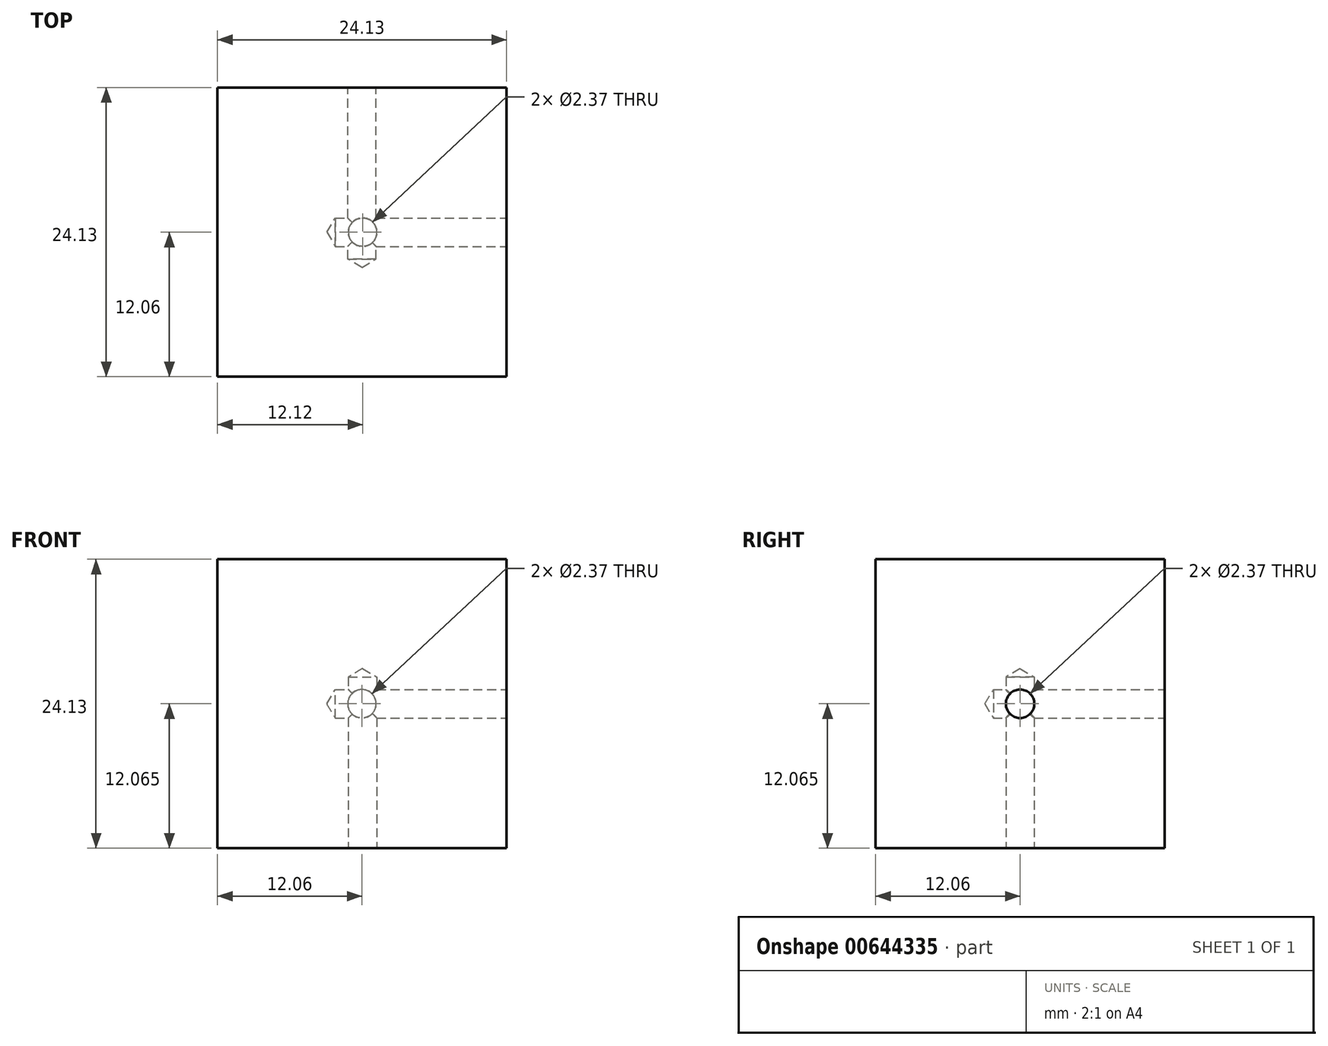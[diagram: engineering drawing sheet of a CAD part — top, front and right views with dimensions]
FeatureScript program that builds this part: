
annotation { "Feature Type Name" : "Feature", "Feature Type Description" : "" }
export const myFeature = defineFeature(function(context is Context, id is Id, definition is map)
    precondition{}
    {
        {
            var Q0;
            Q0=qCreatedBy(makeId("Top.planeOp"),FACE);
            var sketch = newSketch(context, id + "F0", { "sketchPlane" : qUnion([Q0])});
            skLineSegment(sketch, "E0.bottom", {"start": v(-12.06, 12.07) * mm, "end": v(12.07, 12.07) * mm});
            skLineSegment(sketch, "E0.top", {"start": v(-12.06, -12.07) * mm, "end": v(12.06, -12.07) * mm});
            skLineSegment(sketch, "E0.left", {"start": v(-12.06, 12.07) * mm, "end": v(-12.07, -12.06) * mm});
            skLineSegment(sketch, "E0.right", {"start": v(12.06, 12.07) * mm, "end": v(12.06, -12.06) * mm});
            skPoint(sketch, "E0.middle", {"position": v(0, 0) * mm});
            skSolve(sketch);
        }
        {
            var Q0;
            Q0=makeQuery(id+"F0.imprint","IMPRINT",FACE,{"disambiguationData":[TD([[makeQuery(id+"F0.imprint","IMPRINT",EDGE,{"derivedFrom":sQuery(id+"F0.wireOp",EDGE,"E0.bottom")}),-1.0]])]});
            extrude(context, id + "F1", {"entities" : qUnion([Q0]), "depth" : 24.13 * mm, "offsetDistance" : 25.4 * mm});
        }
        {
            var Q0;
            Q0=makeQuery(id+"F1.opExtrude","SWEPT_FACE",FACE,{"disambiguationData":[OSD([sQuery(id+"F0.wireOp",EDGE,"E0.right")])]});
            var sketch = newSketch(context, id + "F2", { "sketchPlane" : qUnion([Q0])});
            skLineSegment(sketch, "E1", {"start": v(0, 0) * mm, "end": v(0, 12.07) * mm});
            skPoint(sketch, "E1.endSnap0", {"position": v(0, 0) * mm});
            skCircle(sketch, "E2", {"center": v(0, 12.07) * mm, "radius": 1.2 * mm});
            skSolve(sketch);
        }
        {
            var Q0;
            Q0=sQuery(id+"F2.wireOp",VERTEX,"E2.center");
            var Q1;
            Q1=makeQuery(id+"F1.opExtrude","SWEPT_BODY",BODY,{"disambiguationData":[OSD([sQuery(id+"F0.wireOp",EDGE,"E0.bottom"),sQuery(id+"F0.wireOp",EDGE,"E0.top"),sQuery(id+"F0.wireOp",EDGE,"E0.left"),sQuery(id+"F0.wireOp",EDGE,"E0.right")])]});
            hole(context, id + "F3", {"style" : HoleStyle.SIMPLE, "endStyle" : HoleEndStyle.BLIND, "standardTappedOrClearance" : lookupTablePath({ "standard" : "ANSI", "engagement" : "75%", "pitch" : "48 tpi", "size" : "#4", "type" : "Tapped" }), "standardBlindInLast" : lookupTablePath({ "standard" : "ANSI", "engagement" : "75%", "pitch" : "48 tpi", "size" : "#4", "type" : "Tapped" }), "holeDiameter" : 2.37 * mm, "majorDiameter" : 2.84 * mm, "showTappedDepth" : true, "holeDepth" : 14.29 * mm, "isTappedThrough" : true, "tappedDepth" : 12.7 * mm, "tapClearance" : 3, "locations" : qUnion([Q0]), "scope" : qUnion([Q1])});
        }
        {
            var Q0;
            Q0=makeQuery(id+"F1.opExtrude","CAP_FACE",FACE,{"disambiguationData":[OSD([sQuery(id+"F0.wireOp",EDGE,"E0.bottom"),sQuery(id+"F0.wireOp",EDGE,"E0.top"),sQuery(id+"F0.wireOp",EDGE,"E0.left"),sQuery(id+"F0.wireOp",EDGE,"E0.right")])],"isStart":true});
            var sketch = newSketch(context, id + "F4", { "sketchPlane" : qUnion([Q0])});
            skLineSegment(sketch, "E3", {"start": v(0.06, 0) * mm, "end": v(0.06, -12.07) * mm});
            skCircle(sketch, "E4", {"center": v(0, 0) * mm, "radius": 1.2 * mm});
            skSolve(sketch);
        }
        {
            var Q0;
            Q0=sQuery(id+"F4.wireOp",VERTEX,"E3.start");
            var Q1;
            Q1=makeQuery(id+"F1.opExtrude","SWEPT_BODY",BODY,{"disambiguationData":[OSD([sQuery(id+"F0.wireOp",EDGE,"E0.bottom"),sQuery(id+"F0.wireOp",EDGE,"E0.top"),sQuery(id+"F0.wireOp",EDGE,"E0.left"),sQuery(id+"F0.wireOp",EDGE,"E0.right")])]});
            hole(context, id + "F5", {"style" : HoleStyle.SIMPLE, "endStyle" : HoleEndStyle.BLIND, "standardTappedOrClearance" : lookupTablePath({ "standard" : "ANSI", "engagement" : "75%", "pitch" : "48 tpi", "size" : "#4", "type" : "Tapped" }), "standardBlindInLast" : lookupTablePath({ "standard" : "ANSI", "engagement" : "75%", "pitch" : "48 tpi", "size" : "#4", "type" : "Tapped" }), "holeDiameter" : 2.37 * mm, "majorDiameter" : 2.84 * mm, "showTappedDepth" : true, "holeDepth" : 14.3 * mm, "isTappedThrough" : true, "tappedDepth" : 12.71 * mm, "tapClearance" : 3, "locations" : qUnion([Q0]), "scope" : qUnion([Q1])});
        }
        {
            var Q0;
            Q0=makeQuery(id+"F1.opExtrude","SWEPT_FACE",FACE,{"disambiguationData":[OSD([sQuery(id+"F0.wireOp",EDGE,"E0.bottom")])]});
            var sketch = newSketch(context, id + "F6", { "sketchPlane" : qUnion([Q0])});
            skLineSegment(sketch, "E5", {"start": v(0, 0) * mm, "end": v(0, 12.07) * mm});
            skPoint(sketch, "E5.endSnap0", {"position": v(0, 0) * mm});
            skSolve(sketch);
        }
        {
            var Q0;
            Q0=sQuery(id+"F6.wireOp",VERTEX,"E5.end");
            var Q1;
            Q1=makeQuery(id+"F1.opExtrude","SWEPT_BODY",BODY,{"disambiguationData":[OSD([sQuery(id+"F0.wireOp",EDGE,"E0.bottom"),sQuery(id+"F0.wireOp",EDGE,"E0.top"),sQuery(id+"F0.wireOp",EDGE,"E0.left"),sQuery(id+"F0.wireOp",EDGE,"E0.right")])]});
            hole(context, id + "F7", {"style" : HoleStyle.SIMPLE, "endStyle" : HoleEndStyle.BLIND, "standardTappedOrClearance" : lookupTablePath({ "standard" : "ANSI", "engagement" : "75%", "pitch" : "48 tpi", "size" : "#4", "type" : "Tapped" }), "standardBlindInLast" : lookupTablePath({ "standard" : "ANSI", "engagement" : "75%", "pitch" : "48 tpi", "size" : "#4", "type" : "Tapped" }), "holeDiameter" : 2.37 * mm, "majorDiameter" : 2.84 * mm, "showTappedDepth" : true, "holeDepth" : 14.3 * mm, "isTappedThrough" : true, "tappedDepth" : 12.71 * mm, "tapClearance" : 3, "locations" : qUnion([Q0]), "scope" : qUnion([Q1])});
        }
    });
